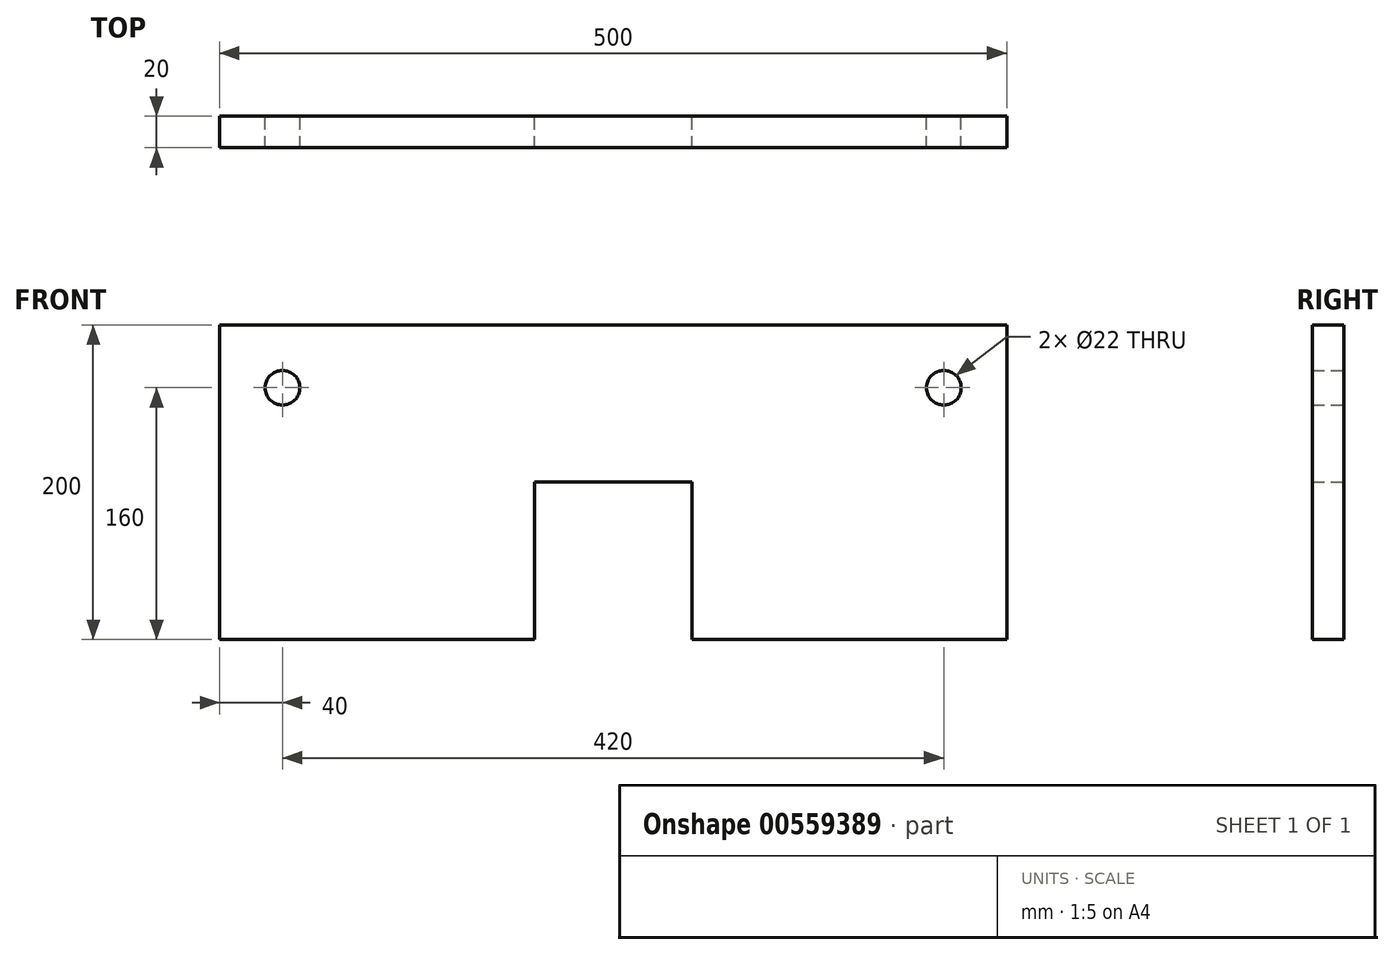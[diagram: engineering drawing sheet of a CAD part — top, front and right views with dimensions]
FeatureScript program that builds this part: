
annotation { "Feature Type Name" : "Feature", "Feature Type Description" : "" }
export const myFeature = defineFeature(function(context is Context, id is Id, definition is map)
    precondition{}
    {
        {
            var Q0;
            Q0=qCreatedBy(makeId("Front.planeOp"),FACE);
            var sketch = newSketch(context, id + "F0", { "sketchPlane" : qUnion([Q0])});
            skLineSegment(sketch, "E0", {"start": v(0, 0) * mm, "end": v(0, 200) * mm});
            skLineSegment(sketch, "E1", {"start": v(0, 200) * mm, "end": v(500, 200) * mm});
            skLineSegment(sketch, "E2", {"start": v(500, 200) * mm, "end": v(500, 0) * mm});
            skLineSegment(sketch, "E3", {"start": v(500, 0) * mm, "end": v(300, 0) * mm});
            skLineSegment(sketch, "E4", {"start": v(300, 0) * mm, "end": v(300, 100) * mm});
            skLineSegment(sketch, "E5", {"start": v(300, 100) * mm, "end": v(200, 100) * mm});
            skLineSegment(sketch, "E6", {"start": v(200, 100) * mm, "end": v(200, 0) * mm});
            skLineSegment(sketch, "E7", {"start": v(200, 0) * mm, "end": v(0, 0) * mm});
            skCircle(sketch, "E8", {"center": v(40, 160) * mm, "radius": 11 * mm});
            skCircle(sketch, "E9", {"center": v(460, 160) * mm, "radius": 11 * mm});
            skSolve(sketch);
        }
        {
            var Q0;
            Q0=makeQuery(id+"F0.imprint","IMPRINT",FACE,{"disambiguationData":[TD([[makeQuery(id+"F0.imprint","IMPRINT",EDGE,{"derivedFrom":sQuery(id+"F0.wireOp",EDGE,"E0")}),-1.0]])]});
            extrude(context, id + "F1", {"entities" : qUnion([Q0]), "depth" : 20 * mm, "offsetDistance" : 25 * mm});
        }
    });
